# Revit family: TD92_ZIP384_AEV003_RVT20_R00
name_source: partatom
category: Mobiliário
units: mm (PartAtom-declared; Revit-internal decimal feet)

## family parameters
Com base no plano de trabalho = Não
Compartilhado = Não
Corte com vazios quando carregada = Não
Número OmniClass = 23.40.20.00
Ponto de cálculo do ambiente = Não
Sempre na vertical = Sim
Título OmniClass = General Furniture and Specialties

## types (1)
- TD92_ZIP384_AEV003_RVT20_R00
    Descrição = Deixe o dia a dia das crianças ainda mais especial e divertido com o Escorregador Infantil Tramontina Zip em Polietileno. Perfeito para fazer parte do quarto ou playground, ele vem em cores vibrantes e é de fácil montagem e encaixe. É indicado para crianças entre 3 a 7 anos e suporta até 30 kg de muita alegria. Sua fabricação é livre de materiais tóxicos, o que permite que as crianças brinquem sem preocupação. Ele ainda pode compor com outras peças infantis Tramontina e é a escolha perfeita tanto para residenciais ou áreas infantis em ambientes comerciais!
    Elevação padrão = 0  [stored 0 ft]
    Fabricante = Tramontina Delta S/A
    Modelo = Escorregador Infantil Tramontina Zip em Polietileno Amarelo e Vermelho
    Nota-chave = 92384003
    URL = https://www.tramontinastore.com

note: [stored X ft] marks values corroborated as IEEE doubles in the binary element streams (Revit-internal decimal feet)
